# Revit family: Plumbing_Joints_Aignep_Male-Tube-Ball-Valve-with-Padlock-90725
name_source: partatom
category: Pipe Accessories
revit_build: Autodesk Revit 2018 (Build: 20170223_1515(x64)
units: mm (PartAtom-declared; Revit-internal decimal feet)

## family parameters
Always vertical = Yes
Cut with Voids When Loaded = No
OmniClass Number = 23.27.43.00
OmniClass Title = Pipe Fittings
Part Type = Valve - Breaks Into
Round Connector Dimension = Use Diameter
Shared = No
Work Plane-Based = No

## types (2) — shared parameters
Assembly Code = D2040100
BIMobject category = Valves
Description = Male-tube ball valve with padlock
Design country = Italy
Edition number = 1
IFC Classification = Pipe Fitting
Keynote = 15410
Lookup Table Name = Valve - Male-Tube Ball Valve With Padlock- 90725
M = 45 mm
Manufacturer = Aignep Spa
Manufacturer country = Italy
Manufacturer name = Aignep Spa
Material main = Brass
Model = 90725
OmniClass Code = 23-27 43 00
OmniClass Description = Pipe Fittings
Product Guid = 1be5c2e3-6151-4410-a219-9e3209744c28
Product Material = AIGNEP - Brass - Yellow
Product SKU = Male-Tube-Ball-Valve-With-Padlock-90725
Product certification = https://www.aignep.com
Product data url = https://www.bimobject.com
Product family = INFINITY
Product group = Valves
Product name = Male-Tube Ball Valve With Padlock - 90725
Product url = https://www.aignep.com
QR code = https://www.bimobject.com
URL = https://www.aignep.com

## per-type parameters (varying)
- D 25: A=16.5 mm  [stored 0.0541339 ft]; B=37 mm  [stored 0.121391 ft]; C=30.8 mm; CH1=41 mm; CH2=35 mm; Diameter=26 mm; E=42.5 mm; F=19.05 mm  [stored 0.0625 ft]; G=106 mm; H=47.5 mm; H Nut 1=11.06 mm  [stored 0.0362861 ft]; H Nut 2=7.097 mm; H1=4.069 mm  [stored 0.0133497 ft]; H2=1.38 mm; H3=8.83 mm  [stored 0.0289698 ft]; I=59.5 mm; L=115.1 mm; L1=17 mm  [stored 0.0557743 ft]; L2=22 mm  [stored 0.0721785 ft]; L3=12.96 mm  [stored 0.0425197 ft]; M Diameter 1=43.5 mm; M Diameter 2=45 mm; Nominal Diameter 01=25.000 mm; Nominal Diameter 02=19.050 mm; Nut Radius 1=21.5 mm; Nut Radius 2=21.5 mm; R=6.154 mm  [stored 0.0201903 ft]; Tick Size 01=20 mm  [stored 0.0656168 ft]; Tick Size 02=15.24 mm
- D 20: A=9.86 mm; B=31 mm; C=29.3 mm; CH1=32 mm  [stored 0.104987 ft]; CH2=30 mm; Diameter=27 mm; E=34.5 mm; F=12.7 mm  [stored 0.0416667 ft]; G=88 mm; H=42 mm; H Nut 1=7.41 mm; H Nut 2=13.957 mm; H1=2.34 mm; H2=0.9 mm  [stored 0.00295276 ft]; H3=7.817 mm; I=50.7 mm; L=99.35 mm; L1=13.35 mm; L2=13.77 mm; L3=14.87 mm; M Diameter 1=37 mm  [stored 0.121391 ft]; M Diameter 2=35.6 mm; Nominal Diameter 01=20.000 mm; Nominal Diameter 02=12.700 mm; Nut Radius 1=17 mm  [stored 0.0557743 ft]; Nut Radius 2=17 mm  [stored 0.0557743 ft]; R=6.548 mm; Tick Size 01=16 mm; Tick Size 02=10.16 mm  [stored 0.0333333 ft]

note: [stored X ft] marks values corroborated as IEEE doubles in the binary element streams (Revit-internal decimal feet)

## geometry (parser evidence)
native form markers: Sweep x8
no freeform markers — native parametric forms only
